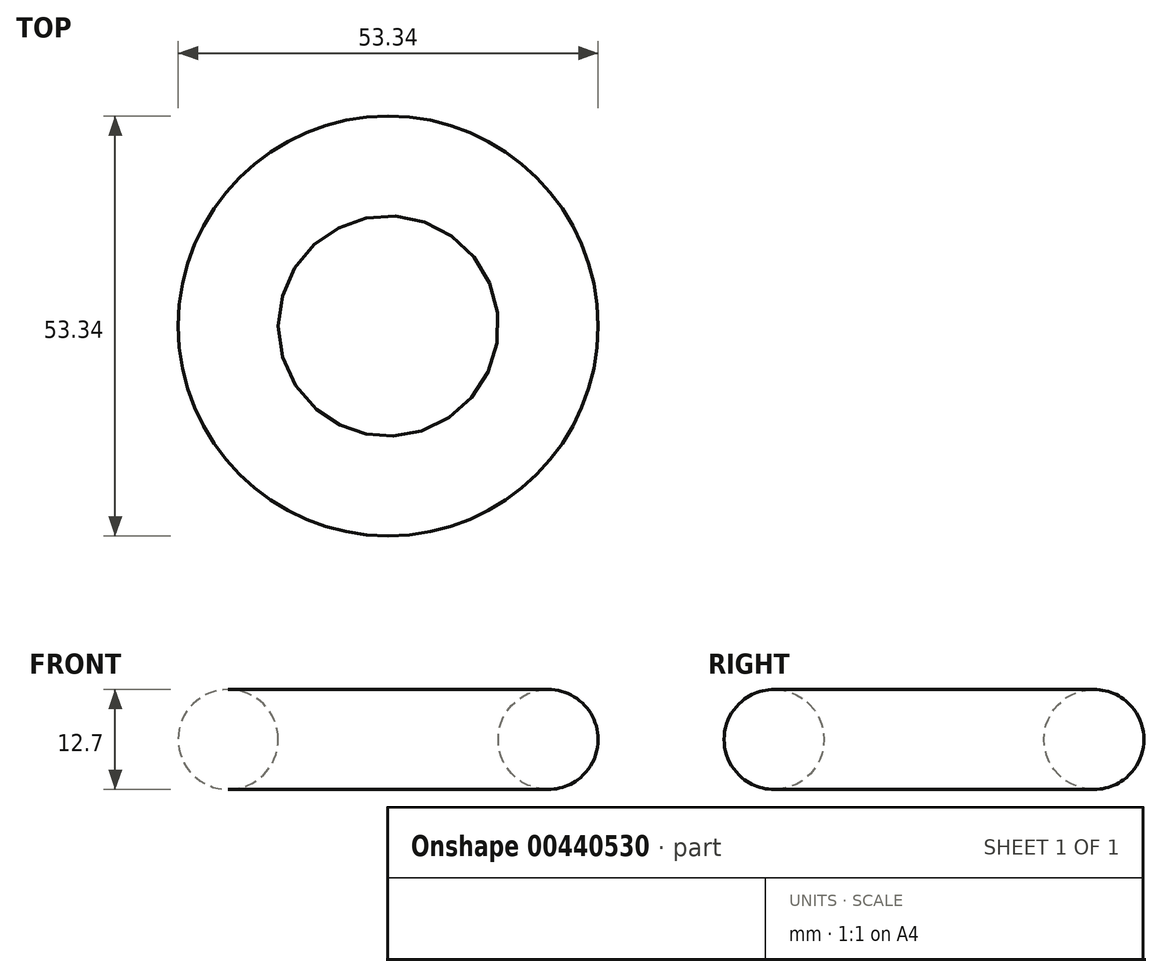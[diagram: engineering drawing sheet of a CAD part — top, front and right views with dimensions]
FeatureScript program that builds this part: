
annotation { "Feature Type Name" : "Feature", "Feature Type Description" : "" }
export const myFeature = defineFeature(function(context is Context, id is Id, definition is map)
    precondition{}
    {
        {
            var Q0;
            Q0=qCreatedBy(makeId("Front.planeOp"),FACE);
            var sketch = newSketch(context, id + "F0", { "sketchPlane" : qUnion([Q0])});
            skCircle(sketch, "E0", {"center": v(20.32, 0) * mm, "radius": 6.35 * mm});
            skLineSegment(sketch, "E1", {"start": v(0, 0) * mm, "end": v(0, 18.4) * mm, "construction": true});
            skSolve(sketch);
        }
        {
            var Q0;
            Q0 = qSketchRegion(id + "F0", true);
            var Q1;
            Q1=sQuery(id+"F0.wireOp",EDGE,"E1");
            revolve(context, id + "F1", {"entities" : qUnion([Q0]), "axis" : qUnion([Q1]), "revolveType" : RevolveType.FULL});
        }
    });
